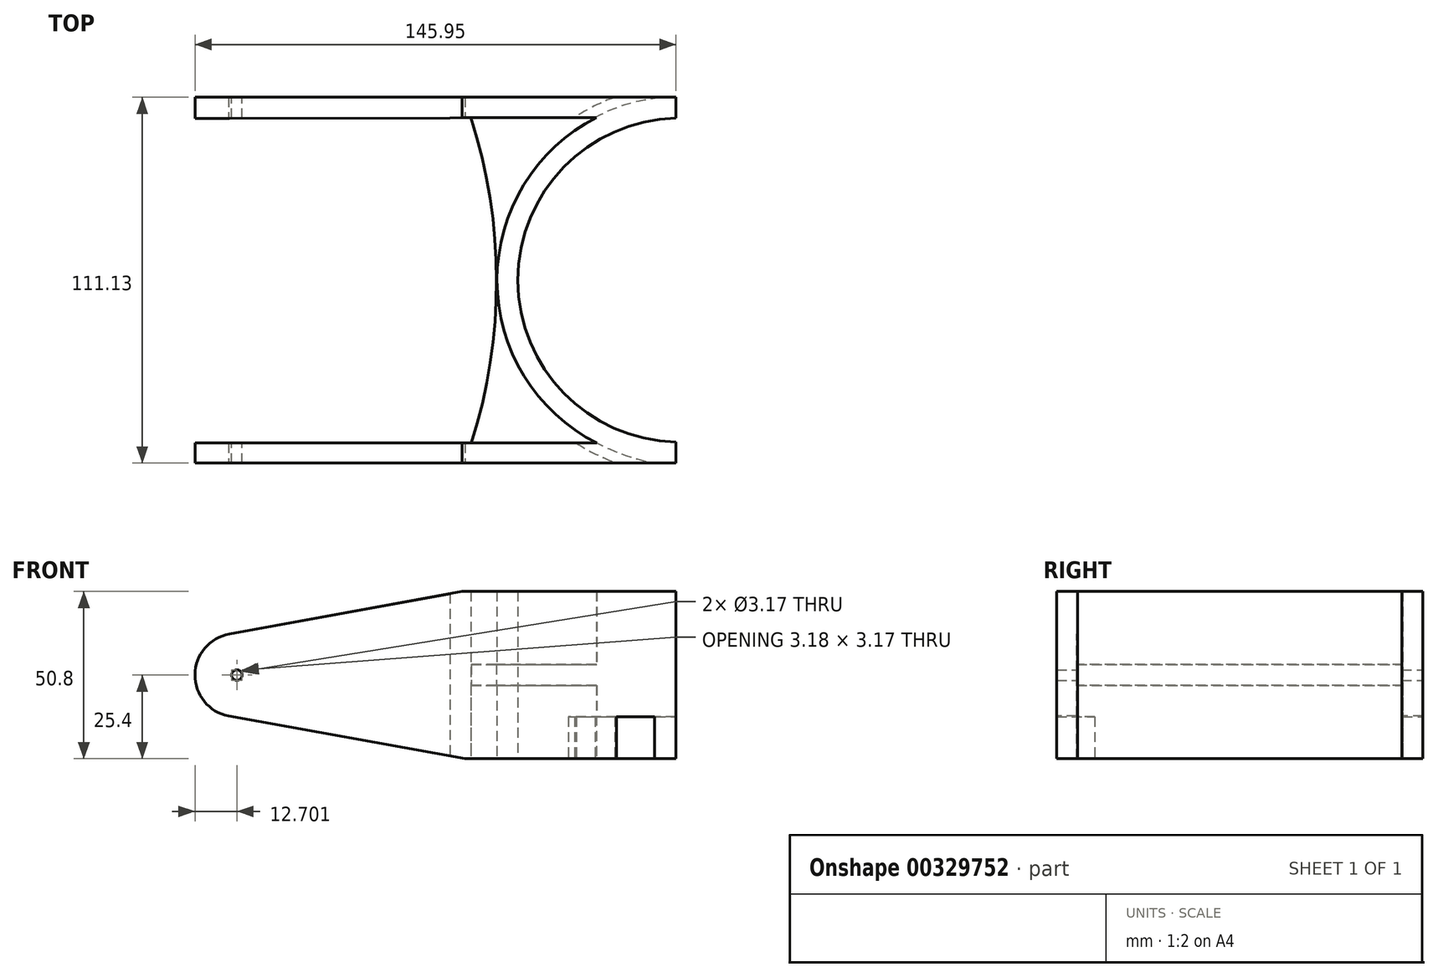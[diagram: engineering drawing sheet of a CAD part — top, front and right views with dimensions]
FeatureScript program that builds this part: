
annotation { "Feature Type Name" : "Feature", "Feature Type Description" : "" }
export const myFeature = defineFeature(function(context is Context, id is Id, definition is map)
    precondition{}
    {
        {
            var Q0;
            Q0=qCreatedBy(makeId("Top.planeOp"),FACE);
            var sketch = newSketch(context, id + "F0", { "sketchPlane" : qUnion([Q0])});
            skArc(sketch, "E0", {"start": v(-1.27, 49.2) * mm, "mid": v(-49.21, 0) * mm, "end": v(-1.27, -49.2) * mm});
            skArc(sketch, "E1.0", {"start": v(-25.41, 49.4) * mm, "mid": v(-55.56, -0.1) * mm, "end": v(-25.23, -49.5) * mm});
            skLineSegment(sketch, "E2", {"start": v(-1.27, 55.55) * mm, "end": v(-1.27, 49.2) * mm});
            skLineSegment(sketch, "E3", {"start": v(0, -49.21) * mm, "end": v(0, -55.56) * mm});
            skLineSegment(sketch, "E4.bottom", {"start": v(-1.27, 55.55) * mm, "end": v(-147.32, 55.55) * mm});
            skLineSegment(sketch, "E4.top", {"start": v(-1.27, -55.58) * mm, "end": v(-147.32, -55.58) * mm});
            skLineSegment(sketch, "E5.trimOffspring", {"start": v(-1.27, -49.2) * mm, "end": v(-1.27, -55.58) * mm});
            skLineSegment(sketch, "E6", {"start": v(-147.32, 55.55) * mm, "end": v(-147.32, 49.1) * mm});
            skLineSegment(sketch, "E7", {"start": v(-147.32, -55.58) * mm, "end": v(-147.32, -49.5) * mm});
            skLineSegment(sketch, "E8", {"start": v(-147.32, -49.5) * mm, "end": v(-25.23, -49.5) * mm});
            skLineSegment(sketch, "E9", {"start": v(-147.32, 49.1) * mm, "end": v(-25.41, 49.4) * mm});
            skLineSegment(sketch, "E10", {"start": v(-63.51, 49.4) * mm, "end": v(-69.86, 49.3) * mm});
            skLineSegment(sketch, "E11", {"start": v(-63.33, -49.5) * mm, "end": v(-69.68, -49.5) * mm});
            skArc(sketch, "E12", {"start": v(-69.68, -49.5) * mm, "mid": v(-61.43, -0.09) * mm, "end": v(-69.86, 49.3) * mm});
            skArc(sketch, "E13", {"start": v(-63.33, -49.5) * mm, "mid": v(-55.7, -0.03) * mm, "end": v(-63.51, 49.4) * mm});
            skLineSegment(sketch, "E14", {"start": v(-69.68, -49.5) * mm, "end": v(-63.33, -49.5) * mm});
            skLineSegment(sketch, "E15", {"start": v(-69.86, 49.3) * mm, "end": v(-63.51, 49.4) * mm});
            skSolve(sketch);
        }
        {
            var Q0;
            {var subQ3=sQuery(id+"F0.wireOp",EDGE,"E4.bottom");Q0=makeQuery(id+"F0.imprint","IMPRINT",FACE,{"disambiguationData":[TD([[makeQuery(id+"F0.imprint","IMPRINT",EDGE,{"derivedFrom":subQ3}),1.0]])]});}
            var Q1;
            {var subQ2=sQuery(id+"F0.wireOp",EDGE,"E4.top");Q1=makeQuery(id+"F0.imprint","IMPRINT",FACE,{"disambiguationData":[TD([[makeQuery(id+"F0.imprint","IMPRINT",EDGE,{"derivedFrom":subQ2}),-1.0]])]});}
            var Q2;
            {var subQ4=sQuery(id+"F0.wireOp",EDGE,"E2");Q2=makeQuery(id+"F0.imprint","IMPRINT",FACE,{"disambiguationData":[TD([[makeQuery(id+"F0.imprint","IMPRINT",EDGE,{"derivedFrom":subQ4}),-1.0]])]});}
            extrude(context, id + "F1", {"entities" : qUnion([Q0, Q1, Q2]), "endBound" : BoundingType.SYMMETRIC, "depth" : 50.8 * mm});
        }
        {
            var Q0;
            Q0=makeQuery(id+"F1.opExtrude","SWEPT_FACE",FACE,{"disambiguationData":[OSD([sQuery(id+"F0.wireOp",EDGE,"E4.top")])]});
            var sketch = newSketch(context, id + "F2", { "sketchPlane" : qUnion([Q0])});
            skSolve(sketch);
        }
        {
            var Q0;
            {var subQ1=sQuery(id+"F0.wireOp",EDGE,"U8nKFDl3-79kX-OwHk-EaO0-BTTa4R9wu8cM");var subQ2=sQuery(id+"F0.wireOp",EDGE,"E1.0");var subQ4=makeQuery(id+"F0.imprint","INTERSECT",VERTEX,{"derivedFrom":[subQ2,subQ1]});Q0=makeQuery(id+"F0.imprint","IMPRINT",FACE,{"disambiguationData":[TD([[makeQuery(id+"F0.imprint","IMPRINT",EDGE,{"disambiguationData":[TD([[subQ4,1.0]])],"derivedFrom":subQ2}),-1.0]])]});}
            var Q1;
            {var subQ0=sQuery(id+"F0.wireOp",EDGE,"Sarp5LDe-epc4-feCA-tBnT-7ws2dZc43zB3");var subQ3=sQuery(id+"F0.wireOp",EDGE,"E13");var subQ5=makeQuery(id+"F0.imprint","INTERSECT",VERTEX,{"derivedFrom":[subQ0,subQ3]});Q1=makeQuery(id+"F0.imprint","IMPRINT",FACE,{"disambiguationData":[TD([[makeQuery(id+"F0.imprint","IMPRINT",EDGE,{"disambiguationData":[TD([[subQ5,-1.0]])],"derivedFrom":subQ0}),-1.0]])]});}
            var Q2;
            Q2=sQuery(id+"F0.wireOp",EDGE,"E14");
            var Q3;
            Q3=sQuery(id+"F0.wireOp",EDGE,"E13");
            var Q4;
            Q4=sQuery(id+"F0.wireOp",EDGE,"E12");
            var Q5;
            Q5=sQuery(id+"F0.wireOp",EDGE,"E10");
            extrude(context, id + "F3", {"entities" : qUnion([Q0, Q1]), "operationType" : NewBodyOperationType.ADD, "surfaceEntities" : qUnion([Q2, Q3, Q4, Q5]), "endBound" : BoundingType.SYMMETRIC, "depth" : 6.35 * mm});
        }
        {
            var Q0;
            {var subQ0=sQuery(id+"F0.wireOp",EDGE,"E4.top");Q0=makeQuery(id+"F2.imprint","IMPRINT",FACE,{"disambiguationData":[TD([[makeQuery(id+"F2.imprint","IMPRINT",EDGE,{"derivedFrom":makeQuery(id+"F1.opExtrude","CAP_EDGE",EDGE,{"disambiguationData":[OSD([subQ0])],"isStart":true})}),-1.0]])]});}
            var sketch = newSketch(context, id + "F4", { "sketchPlane" : qUnion([Q0])});
            skArc(sketch, "E16", {"start": v(-136.8, 12.5) * mm, "mid": v(-147.22, 0.14) * mm, "end": v(-137.07, -12.44) * mm});
            skLineSegment(sketch, "E17", {"start": v(-136.8, 12.5) * mm, "end": v(-64.67, 25.67) * mm});
            skLineSegment(sketch, "E18.bottom", {"start": v(-147.4, -25.5) * mm, "end": v(-64.67, -25.5) * mm});
            skLineSegment(sketch, "E18.top", {"start": v(-147.4, 25.67) * mm, "end": v(-64.67, 25.67) * mm});
            skLineSegment(sketch, "E18.left", {"start": v(-147.4, -25.5) * mm, "end": v(-147.4, 25.67) * mm});
            skLineSegment(sketch, "E18.right", {"start": v(-64.67, -25.5) * mm, "end": v(-64.67, 25.67) * mm});
            skLineSegment(sketch, "E19", {"start": v(-137.07, -12.44) * mm, "end": v(-64.67, -25.5) * mm});
            skSolve(sketch);
        }
        {
            var Q0;
            {var subQ3=sQuery(id+"F4.wireOp",EDGE,"E16");Q0=makeQuery(id+"F4.imprint","IMPRINT",FACE,{"disambiguationData":[TD([[makeQuery(id+"F4.imprint","IMPRINT",EDGE,{"derivedFrom":subQ3}),-1.0]])]});}
            extrude(context, id + "F5", {"entities" : qUnion([Q0]), "operationType" : NewBodyOperationType.REMOVE, "depth" : -120.65 * mm});
        }
        {
            var Q0;
            {var subQ0=sQuery(id+"F0.wireOp",EDGE,"E2");Q0=makeQuery(id+"FksFuFTW7cVjso9_0.boolean.opBoolean","MERGE",FACE,{"derivedFrom":[makeQuery(id+"F1.opExtrude","CAP_FACE",FACE,{"disambiguationData":[OSD([sQuery(id+"F0.wireOp",EDGE,"E0"),sQuery(id+"F0.wireOp",EDGE,"E1.0"),sQuery(id+"F0.wireOp",EDGE,"E4.bottom"),sQuery(id+"F0.wireOp",EDGE,"E4.top"),sQuery(id+"F0.wireOp",EDGE,"E5.trimOffspring"),sQuery(id+"F0.wireOp",EDGE,"E6"),sQuery(id+"F0.wireOp",EDGE,"E7"),sQuery(id+"F0.wireOp",EDGE,"E8"),sQuery(id+"F0.wireOp",EDGE,"E9"),sQuery(id+"F0.wireOp",EDGE,"E13"),sQuery(id+"F0.wireOp",EDGE,"E14"),sQuery(id+"F0.wireOp",EDGE,"E15"),subQ0])],"isStart":true}),makeQuery(id+"FksFuFTW7cVjso9_0.opExtrude","CAP_FACE",FACE,{"disambiguationData":[OSD([sQuery(id+"F0.wireOp",EDGE,"lKrl4AKN-3JCl-ubzo-q9eR-vsdmown4jFDz"),sQuery(id+"F0.wireOp",EDGE,"yNrtJNle-V6xo-H4dn-AFSr-d2MaLDmPO5EE"),subQ0,sQuery(id+"F0.wireOp",EDGE,"E3"),sQuery(id+"F0.wireOp",EDGE,"EES77Svr-PVDO-xaoS-e9ec-JAbvYg96hIdu"),sQuery(id+"F0.wireOp",EDGE,"x2OGRPyS-xJFL-3bE6-5xDx-OpvrhpVSOPwl"),sQuery(id+"F0.wireOp",EDGE,"LQq3tHfn-6ljx-p5u7-Qabu-EdWBv65WH1yn")])],"isStart":true})]});}
            var sketch = newSketch(context, id + "F6", { "sketchPlane" : qUnion([Q0])});
            skArc(sketch, "E20", {"start": v(-7.77, 55.58) * mm, "mid": v(-21.45, 51.3) * mm, "end": v(-33.84, 44.07) * mm});
            skArc(sketch, "E21.0", {"start": v(-8.37, 58.7) * mm, "mid": v(-22.73, 54.2) * mm, "end": v(-35.74, 46.62) * mm});
            skLineSegment(sketch, "E22", {"start": v(-7.77, 55.58) * mm, "end": v(-8.37, 58.7) * mm});
            skLineSegment(sketch, "E23", {"start": v(-35.74, 46.62) * mm, "end": v(-33.84, 44.07) * mm});
            skArc(sketch, "E24", {"start": v(-35.5, -42.74) * mm, "mid": v(-19.54, -52.24) * mm, "end": v(-1.27, -55.55) * mm});
            skArc(sketch, "E25.0", {"start": v(-37.58, -45.14) * mm, "mid": v(-20.65, -55.22) * mm, "end": v(-1.27, -58.72) * mm});
            skLineSegment(sketch, "E26", {"start": v(-37.58, -45.14) * mm, "end": v(-35.5, -42.74) * mm});
            skLineSegment(sketch, "E27", {"start": v(-1.27, -58.72) * mm, "end": v(-1.27, -55.55) * mm});
            skSolve(sketch);
        }
        {
            var Q0;
            {var subQ0=sQuery(id+"F6.wireOp",EDGE,"E20");Q0=makeQuery(id+"F6.imprint","IMPRINT",FACE,{"disambiguationData":[TD([[makeQuery(id+"F6.imprint","IMPRINT",EDGE,{"derivedFrom":subQ0}),-1.0]])]});}
            var Q1;
            {var subQ1=makeQuery(id+"F1.opExtrude","CAP_EDGE",EDGE,{"disambiguationData":[OSD([sQuery(id+"F0.wireOp",EDGE,"E4.bottom")])],"isStart":true});var subQ6=sQuery(id+"F6.wireOp",EDGE,"E25.0");var subQ8=makeQuery(id+"F6.imprint","INTERSECT",VERTEX,{"derivedFrom":[subQ1,subQ6]});Q1=makeQuery(id+"F6.imprint","IMPRINT",FACE,{"disambiguationData":[TD([[makeQuery(id+"F6.imprint","IMPRINT",EDGE,{"disambiguationData":[TD([[subQ8,1.0]])],"derivedFrom":subQ6}),1.0]])]});}
            extrude(context, id + "F7", {"entities" : qUnion([Q0, Q1]), "operationType" : NewBodyOperationType.REMOVE, "oppositeDirection" : true, "depth" : 12.7 * mm});
        }
        {
            var Q0;
            Q0=makeQuery(id+"F1.opExtrude","SWEPT_FACE",FACE,{"disambiguationData":[OSD([sQuery(id+"F0.wireOp",EDGE,"E4.bottom")])]});
            var sketch = newSketch(context, id + "F8", { "sketchPlane" : qUnion([Q0])});
            skCircle(sketch, "E28", {"center": v(134.52, 0) * mm, "radius": 1.59 * mm});
            skSolve(sketch);
        }
        {
            var Q0;
            Q0 = qSketchRegion(id + "F8", true);
            extrude(context, id + "F9", {"entities" : qUnion([Q0]), "operationType" : NewBodyOperationType.REMOVE, "oppositeDirection" : true, "depth" : 121.92 * mm});
        }
    });
